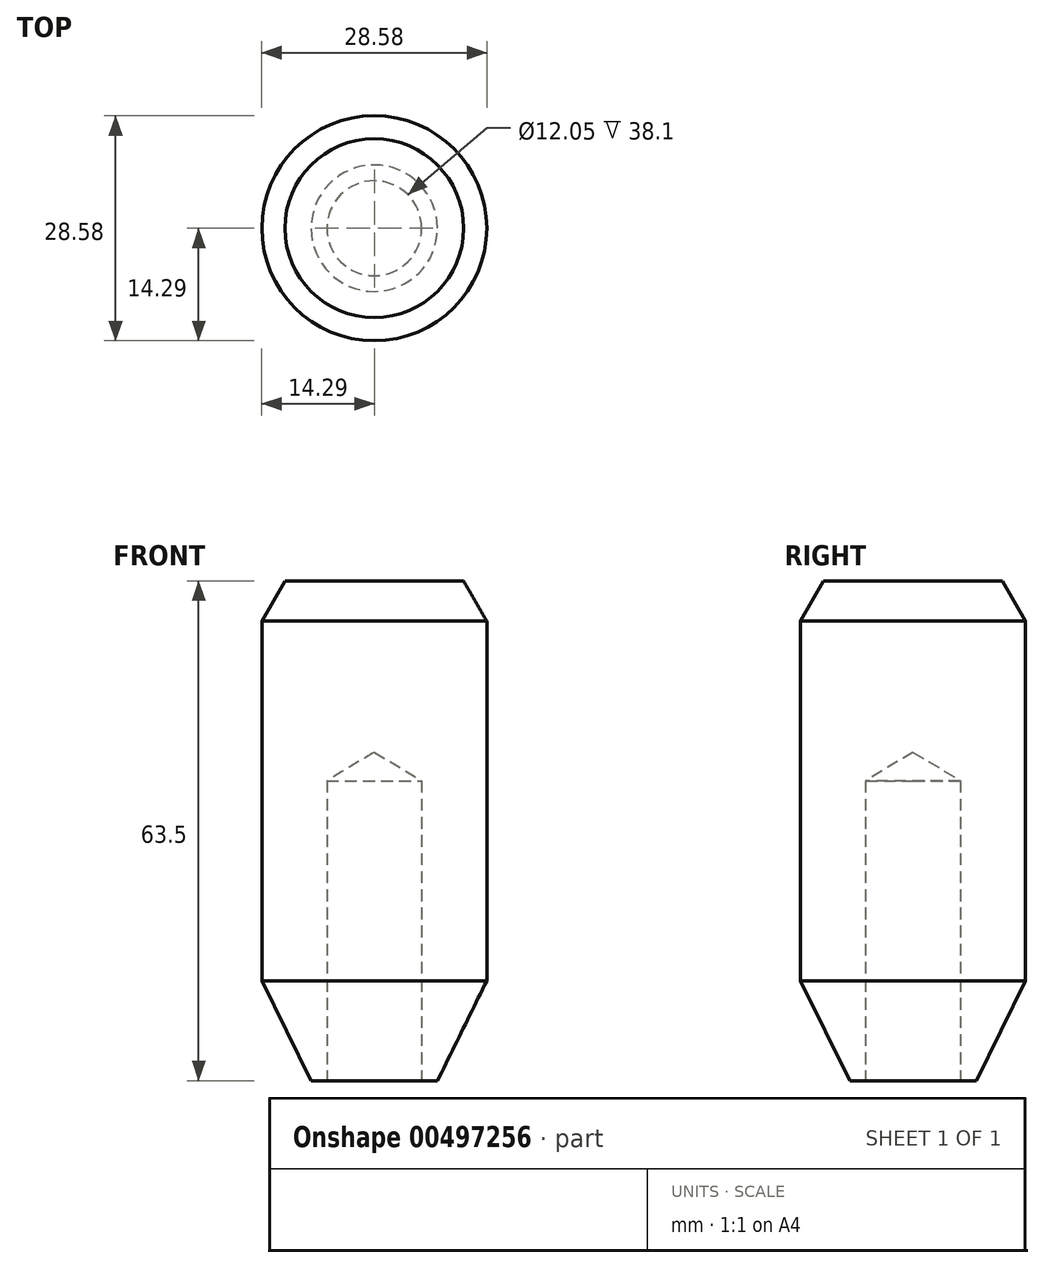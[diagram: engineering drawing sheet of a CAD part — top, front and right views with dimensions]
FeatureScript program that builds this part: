
annotation { "Feature Type Name" : "Feature", "Feature Type Description" : "" }
export const myFeature = defineFeature(function(context is Context, id is Id, definition is map)
    precondition{}
    {
        {
            var Q0;
            Q0=qCreatedBy(makeId("Top.planeOp"),FACE);
            var sketch = newSketch(context, id + "F0", { "sketchPlane" : qUnion([Q0])});
            skCircle(sketch, "E0", {"center": v(0, 0) * mm, "radius": 8.03 * mm});
            skSolve(sketch);
        }
        {
            var Q0;
            Q0=qCreatedBy(makeId("Top.planeOp"),FACE);
            cPlane(context, id + "F1", {"entities" : qUnion([Q0]), "cplaneType" : CPlaneType.OFFSET, "offset" : 12.7 * mm, "width" : 152.4 * mm, "height" : 152.4 * mm});
        }
        {
            var Q0;
            Q0=qCreatedBy(id+"F1.planeOp",FACE);
            var sketch = newSketch(context, id + "F2", { "sketchPlane" : qUnion([Q0])});
            skCircle(sketch, "E1", {"center": v(0, 0) * mm, "radius": 14.29 * mm});
            skSolve(sketch);
        }
        {
            var Q0;
            Q0=qCreatedBy(id+"F1.planeOp",FACE);
            cPlane(context, id + "F3", {"entities" : qUnion([Q0]), "cplaneType" : CPlaneType.OFFSET, "offset" : 50.8 * mm, "width" : 152.4 * mm, "height" : 152.4 * mm});
        }
        {
            var Q0;
            Q0=qCreatedBy(id+"F3.planeOp",FACE);
            var sketch = newSketch(context, id + "F4", { "sketchPlane" : qUnion([Q0])});
            skCircle(sketch, "E2", {"center": v(0, 0) * mm, "radius": 14.29 * mm});
            skSolve(sketch);
        }
        {
            var Q0;
            Q0=makeQuery(id+"F0.imprint","IMPRINT",FACE,{"disambiguationData":[TD([[makeQuery(id+"F0.imprint","IMPRINT",EDGE,{"derivedFrom":sQuery(id+"F0.wireOp",EDGE,"E0")}),1.0]])]});
            var Q1;
            Q1=makeQuery(id+"F2.imprint","IMPRINT",FACE,{"disambiguationData":[TD([[makeQuery(id+"F2.imprint","IMPRINT",EDGE,{"derivedFrom":sQuery(id+"F2.wireOp",EDGE,"E1")}),1.0]])]});
            loft(context, id + "F5", {"sheetProfilesArray" : [{ "sheetProfileEntities" : qUnion([Q0]) }, { "sheetProfileEntities" : qUnion([Q1]) }]});
        }
        {
            var Q1;
            Q1=makeQuery(id+"F4.imprint","IMPRINT",FACE,{"disambiguationData":[TD([[makeQuery(id+"F4.imprint","IMPRINT",EDGE,{"derivedFrom":sQuery(id+"F4.wireOp",EDGE,"E2")}),1.0]])]});
            var Q2;
            Q2 = qSketchRegion(id + "F2", true);
            loft(context, id + "F6", {"operationType" : NewBodyOperationType.ADD, "sheetProfilesArray" : [{ "sheetProfileEntities" : qUnion([Q1]) }, { "sheetProfileEntities" : qUnion([Q2]) }]});
        }
        {
            var Q0;
            Q0=makeQuery(id+"F5.opLoft","CAP_FACE",FACE,{"disambiguationData":[OSD([makeQuery(id+"F0.imprint","IMPRINT",FACE,{"disambiguationData":[TD([[makeQuery(id+"F0.imprint","IMPRINT",EDGE,{"derivedFrom":sQuery(id+"F0.wireOp",EDGE,"E0")}),1.0]])]})])],"isStart":true});
            var sketch = newSketch(context, id + "F7", { "sketchPlane" : qUnion([Q0])});
            skPoint(sketch, "E3", {"position": v(0, 0) * mm});
            skSolve(sketch);
        }
        {
            var Q0;
            Q0=sQuery(id+"F7.wireOp",VERTEX,"E3");
            var Q1;
            Q1=makeQuery(id+"F5.opLoft","SWEPT_BODY",BODY,{"disambiguationData":[OSD([makeQuery(id+"F0.imprint","IMPRINT",FACE,{"disambiguationData":[TD([[makeQuery(id+"F0.imprint","IMPRINT",EDGE,{"derivedFrom":sQuery(id+"F0.wireOp",EDGE,"E0")}),1.0]])]}),makeQuery(id+"F2.imprint","IMPRINT",FACE,{"disambiguationData":[TD([[makeQuery(id+"F2.imprint","IMPRINT",EDGE,{"derivedFrom":sQuery(id+"F2.wireOp",EDGE,"E1")}),1.0]])]})])]});
            hole(context, id + "F8", {"style" : HoleStyle.SIMPLE, "endStyle" : HoleEndStyle.BLIND, "holeDiameter" : 12.05 * mm, "holeDepth" : 38.1 * mm, "isTappedThrough" : true, "tappedDepth" : 12.7 * mm, "tapClearance" : 3, "startFromSketch" : true, "locations" : qUnion([Q0]), "scope" : qUnion([Q1])});
        }
        {
            var Q0;
            Q0=makeQuery(id+"F6.opLoft","MID_CAP_EDGE",EDGE,{"disambiguationData":[OSD([sQuery(id+"F4.wireOp",EDGE,"E2")])],"capPos":0.0});
            chamfer(context, id + "F9", {"entities" : qUnion([Q0]), "chamferType" : ChamferType.OFFSET_ANGLE, "width" : 5.08 * mm, "oppositeDirection" : false, "angle" : 30 * degree, "tangentPropagation" : true});
        }
    });
